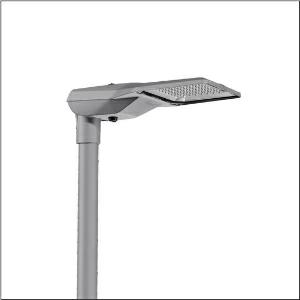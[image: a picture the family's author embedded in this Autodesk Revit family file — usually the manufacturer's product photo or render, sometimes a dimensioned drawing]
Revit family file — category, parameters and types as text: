
# Revit family: streetlight_sl_21_midi___st1_0a_5xe3d63t08lb_b124
name_source: partatom
category: Lighting Fixtures
units: mm (PartAtom-declared; Revit-internal decimal feet)

## family parameters
Cut with Voids When Loaded = No
Host = Face
Light Source = No
Part Type = Normal
Room Calculation Point = No
Round Connector Dimension = Use Diameter
Shared = No

## types (1)
- --- (1 x LED, 12860 lm, 98.3 W, 2700K)
    Apparent Load = 98 VA
    CIE Flux Codes = 37 72 97 100 100
    Color Rendering = 70
    Color Temperature = 2700K
    Default Elevation = 1800 mm
    Description = Streetlight SL 21 midi, mast luminaire, primary light control with lens, of PMMA, primary optical cover: cover, of toughened safety glass, transparent, light distribution: ST1.0a, light emission: direct distribution, primary light characteristic: asymmetric, installation type: side-entry, post-top, LED, High Power LED, rated luminous flux: 12.860lm, luminous efficacy: 131lm/W, light colour: 727, colour temperature: 2700K, control: overheat protection, constant luminous flux control, time-dependent luminous flux control, flexible luminous flux parameterisation, presetting dimming logarithmic, mains connection: 230..240V, AC, 50/60Hz, start of lifetime: 98W, end of service life: 101W, reduction: 45W, luminaire housing, of diecast aluminium, powder-coated, Siteco® metallic grey (DB 702S), corrosivity category C5 mid according to DIN EN ISO 12944, please order mast flange separately, inclination adjustable: 0°, 5°, 10°, 15°, sealing non-destructively replaceable, multi-level sealing system, length: 644mm, width: 335mm, height: 110mm, mast flange for spigot size: 42mm (side-entry): 5XC10008XM4, 60/48mm (side-entry/post-top): 5XC10108XM2, 76/60mm (side-entry/post-top): 5XC10108XM1, Smart Interface below and above, protection rating (complete): IP66, insulation class (complete): insulation class II (safety insulation), certification: CE, ENEC, ENEC+, VDE, impact resistance: IK09, permissible operating ambient temperature for outdoor applications: -40..+50°C, standard-compliant lighting for roads and squares, packaging unit: 1 piece

Light Distribution: ST1.0a
    Height = 111 mm
    Lamp = 1 x LED
    Lamp Light Flux = 12860 lm
    Lamp Power = 98.3 W
    Lamp count = 1
    Length = 644 mm
    Luminous efficacy = 131 lm/W
    Manufacturer = Siteco
    ModVariant = No
    Model = 5XE3D63T08LB
    Number of Poles = 1
    OnlyDefault = Yes
    Power Factor = 1
    Product Name = Streetlight SL 21 midi | ST1.0a
    Product group = mast luminaire | pylon top
    ProductGroupID = 6100
    Protection Class = Protection class II
    Protection Degree = IP 66
    RLX_Detail_Level = 1
    RLX_Emergency_Light_Flux = 0 lm
    RLX_Emergency_Type = 0
    RLX_Emergency_Type_DB = No
    RlxData = <blob elided: 90681 chars, md5=997e6df4>
    Socket = socket
    Standby Power = 0 W
    System Light Flux = 12860 lm
    System Power = 98 W
    Type Comments = factory setting: luminous flux: 100 % | dim-lin: 254 | 1020 mA
    Type Image = l_1004304.jpg
    URL = http://relux.com
    VarID = @adj_141363
    Voltage = 0 V
    Weight = 0.00 kg
    Width = 336 mm

## geometry (parser evidence)
native form markers: Blend x4, Sweep x10
no freeform markers — native parametric forms only
